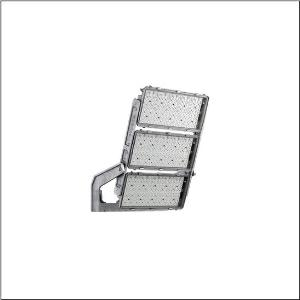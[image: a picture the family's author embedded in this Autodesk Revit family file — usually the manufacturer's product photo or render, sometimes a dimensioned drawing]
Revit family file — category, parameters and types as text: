
# Revit family: floodlight_fl_11_maxi_pro_remote___pl52_5xa779427d01ba_83dd
name_source: partatom
category: Lighting Fixtures
units: mm (PartAtom-declared; Revit-internal decimal feet)

## family parameters
Cut with Voids When Loaded = No
Host = Face
Light Source = No
Part Type = Normal
Room Calculation Point = No
Round Connector Dimension = Use Diameter
Shared = No

## types (1)
- --- (1 x LED, 148130 lm, 1095.9 W, 5000K)
    Apparent Load = 1096 VA
    CIE Flux Codes = 24 55 98 100 100
    Color Rendering = 70
    Color Temperature = 5000K
    Default Elevation = 1800 mm
    Description = Floodlight FL 11  maxi  pro Remote floodlight; light control with lens of PMMA; cover panel of toughened safety glass, transparent; light distribution: PL52, asymmetric direct distribution, LEDcolour temperature: 5000K, rated luminous flux: 148.130lm, colour rendering: CRI > 70, light colour: 750; luminous efficacy: 135lm/W; brightness control: DALI 2 (1 DALI address); with terminal, 8-pole, max. 2.5mm², mains connection: 220..240V/380..400V AC, 50/60Hz, surge voltage resistance: line to ground: 10kV, ECG replaceable separately, LED unit replaceable without ESD environment, dustproof LED module, dimming range 10..100%, no afterglow with DALI off / DMX off command; 1096W floodlight with 3x LED unit of diecast aluminium, coated grey; length: 713mm / width: 651mm / height: 338mm; mounting bracket, of diecast aluminium, uncoated, natural, equipment: Power, protection rating (complete): IP66; insulation class (complete): insulation class I (protective earthing); certification: CE, ENEC, VDE; ball protection: ball impact resistance with accessories, impact resistance: IK07; rated ambient temperature 10°C, only for outdoor installations, permissible operating ambient temperature: -40..+40°C, permissible storage temperature: -40..+85°C; packaging unit: 1 piece

Light Distribution: PL52
    Height = 320 mm
    Lamp = 1 x LED
    Lamp Light Flux = 148130 lm
    Lamp Power = 1095.9 W
    Lamp count = 1
    Length = 1002 mm
    Luminous efficacy = 135 lm/W
    Manufacturer = Siteco
    ModVariant = No
    Model = 5XA779427D01BA
    Mounting Place = Ceiling
    Mounting Type = Surface mounted
    Number of Poles = 1
    OnlyDefault = Yes
    Power Factor = 1
    Product Name = Floodlight FL 11 maxi pro Remote | PL52
    Product group = floodlight | ceiling mounted
    ProductGroupID = 302
    Protection Class = Protection class I
    Protection Degree = IP 66
    RLX_Detail_Level = 1
    RLX_Emergency_Light_Flux = 0 lm
    RLX_Emergency_Type = 0
    RLX_Emergency_Type_DB = No
    RlxData = <blob elided: 52549 chars, md5=1fb554ac>
    Socket = socket
    Standby Power = 0 W
    System Light Flux = 148130 lm
    System Power = 1096 W
    Type Comments = factory setting: luminous flux: 100 % | dim-lin: 254 | 760 mA
    Type Image = l_1006784.jpg
    URL = http://relux.com
    VarID = @adj_028233
    Voltage = 0 V
    Weight = 0.00 kg
    Width = 655 mm

## geometry (parser evidence)
native form markers: Blend x4, Sweep x15
no freeform markers — native parametric forms only
